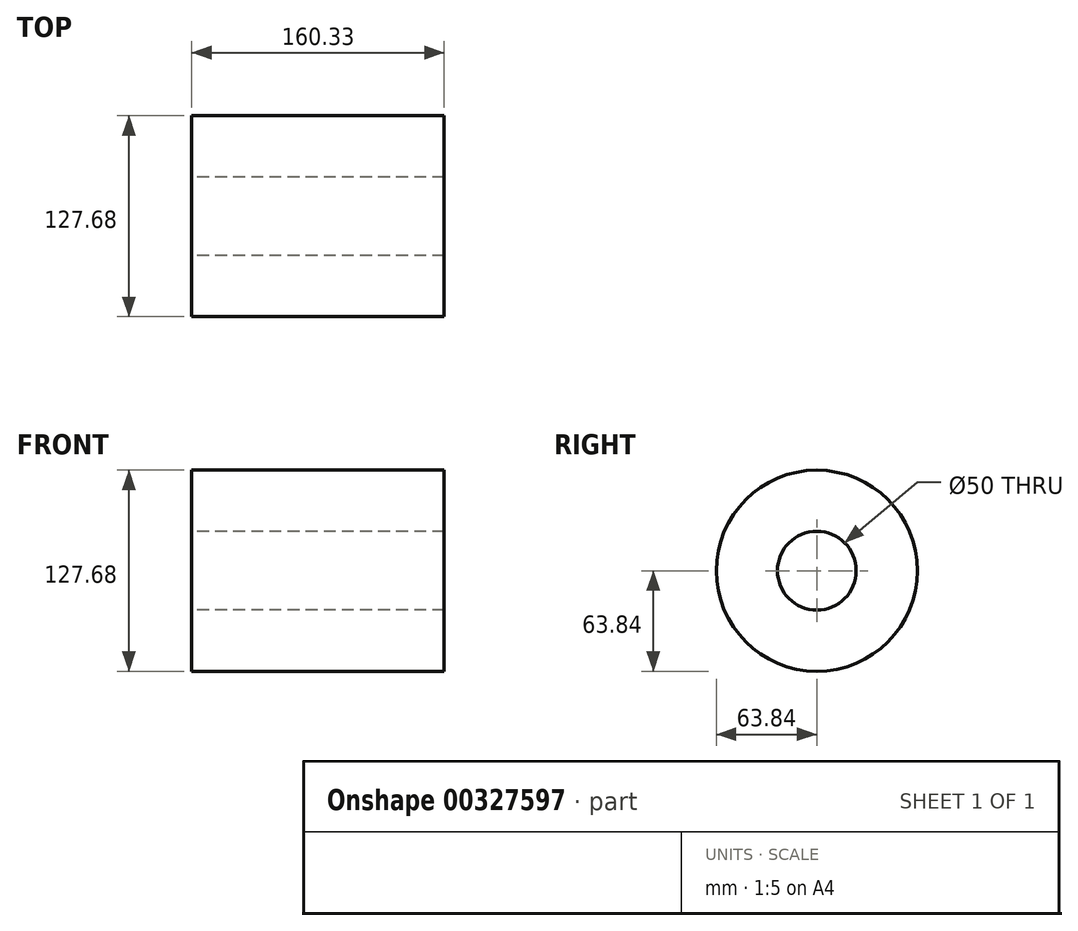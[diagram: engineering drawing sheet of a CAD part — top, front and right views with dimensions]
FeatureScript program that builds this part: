
annotation { "Feature Type Name" : "Feature", "Feature Type Description" : "" }
export const myFeature = defineFeature(function(context is Context, id is Id, definition is map)
    precondition{}
    {
        {
            var Q0;
            Q0=qCreatedBy(makeId("Front.planeOp"),FACE);
            var sketch = newSketch(context, id + "F0", { "sketchPlane" : qUnion([Q0])});
            skLineSegment(sketch, "E0", {"start": v(-66.12, 0) * mm, "end": v(133.06, 0) * mm, "construction": true});
            skLineSegment(sketch, "E1.bottom", {"start": v(-66.94, 63.84) * mm, "end": v(93.39, 63.84) * mm});
            skLineSegment(sketch, "E1.top", {"start": v(-66.94, 25) * mm, "end": v(93.39, 25) * mm});
            skLineSegment(sketch, "E1.left", {"start": v(-66.94, 63.84) * mm, "end": v(-66.94, 25) * mm});
            skLineSegment(sketch, "E1.right", {"start": v(93.39, 63.84) * mm, "end": v(93.39, 25) * mm});
            skSolve(sketch);
        }
        {
            var Q0;
            Q0 = qSketchRegion(id + "F0", true);
            var Q1;
            Q1=sQuery(id+"F0.wireOp",EDGE,"E0");
            revolve(context, id + "F1", {"entities" : qUnion([Q0]), "axis" : qUnion([Q1]), "revolveType" : RevolveType.FULL});
        }
    });
